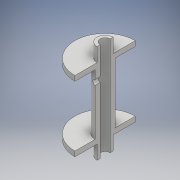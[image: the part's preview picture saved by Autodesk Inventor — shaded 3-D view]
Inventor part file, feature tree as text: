
AUTODESK INVENTOR PART (.ipt)
format: ipt  version: 2017 (Build 210142000, 142)  size: 148,480 bytes
history: native  units: mm
features: sketch x3, extrude x2, revolve x1
ambient origin geometry x8: Origin, YZ Plane, XZ Plane, XY Plane, X Axis, Y Axis, Z Axis, Center Point
bodies: Solid1 (feature_tree)
feature tree (6):
  revolve  "Revolution1"  [1 undecoded]
  extrude  "Extrusion1"  Depth=4.0mm
  extrude  "Extrusion2"  Depth=2.5mm
  sketch  "Sketch1"  dims[d0=2.5mm d1=7.0mm]
  sketch  "Sketch2"  dims[d2=90.0deg d3=4.0mm]
  sketch  "Sketch3"  dims[d4=12.5mm d5=2.5mm d6=2.5mm d7=30.0mm d8=90.0deg d9=15.0mm d10=90.0deg d11=2.5mm d12=10.0mm d13=0.0mm d14=100.0mm d15=0.0mm]
note: 1 required parameter value undecoded (feature->parameter linkage not recoverable at this tier; creation-order binding heuristic only, values carry confidence <= 0.55)
